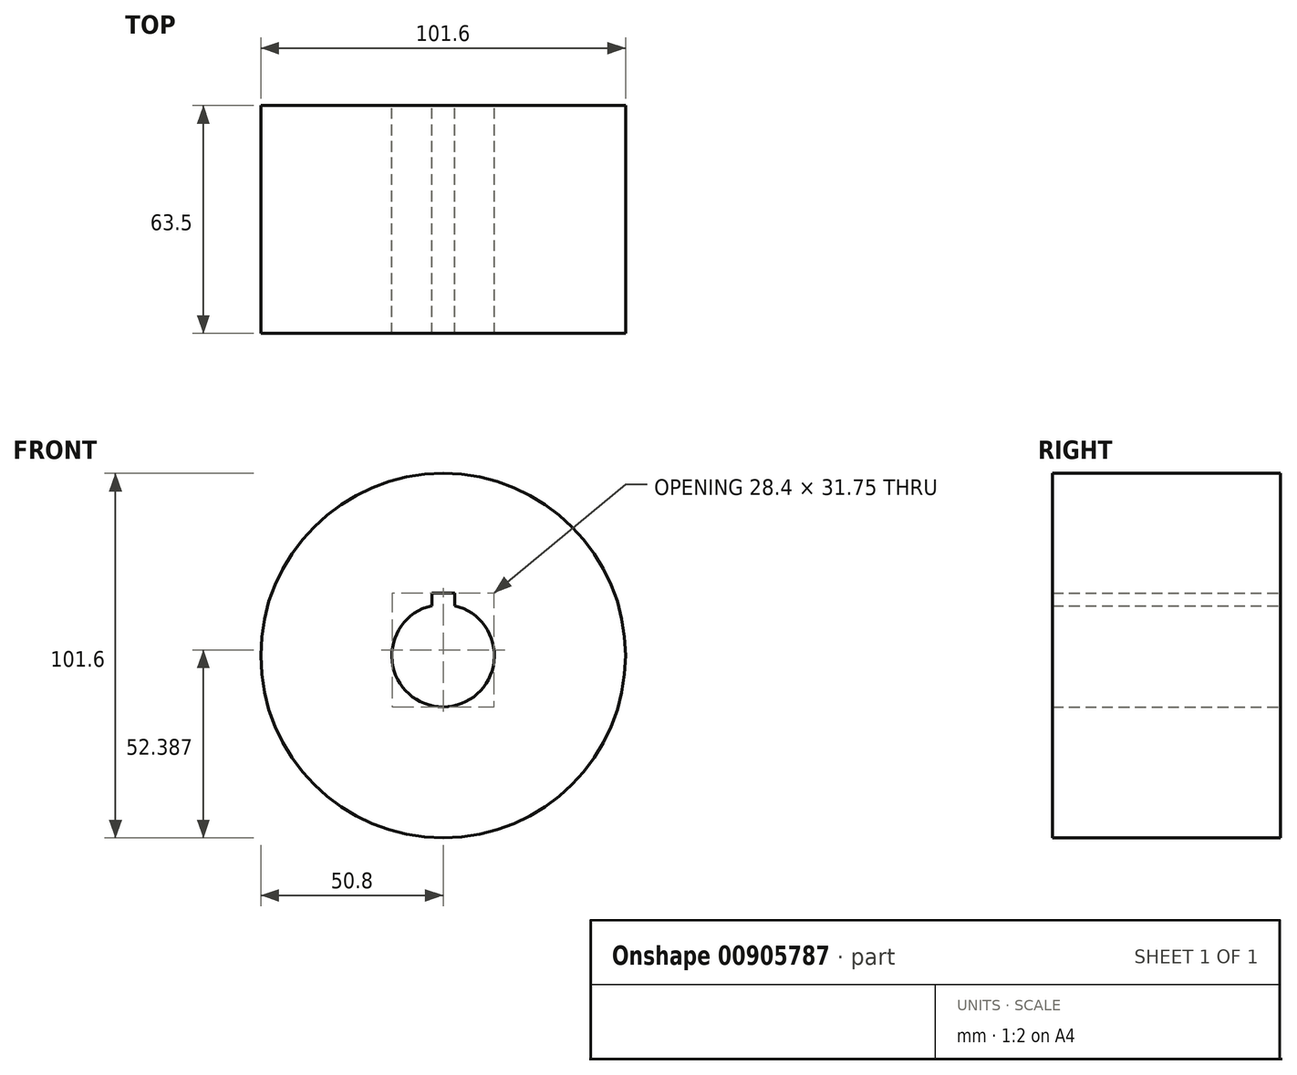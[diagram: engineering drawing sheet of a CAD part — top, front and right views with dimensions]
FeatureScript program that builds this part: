
annotation { "Feature Type Name" : "Feature", "Feature Type Description" : "" }
export const myFeature = defineFeature(function(context is Context, id is Id, definition is map)
    precondition{}
    {
        {
            var Q0;
            Q0=qCreatedBy(makeId("Front.planeOp"),FACE);
            var sketch = newSketch(context, id + "F0", { "sketchPlane" : qUnion([Q0])});
            skCircle(sketch, "E0", {"center": v(0, 0) * mm, "radius": 50.8 * mm});
            skArc(sketch, "E1", {"start": v(-3.18, 13.93) * mm, "mid": v(0, -14.29) * mm, "end": v(3.18, 13.93) * mm});
            skLineSegment(sketch, "E2.top", {"start": v(-3.18, 17.46) * mm, "end": v(3.18, 17.46) * mm});
            skLineSegment(sketch, "E2.left", {"start": v(-3.18, 13.93) * mm, "end": v(-3.18, 17.46) * mm});
            skLineSegment(sketch, "E2.right", {"start": v(3.17, 13.93) * mm, "end": v(3.17, 17.46) * mm});
            skPoint(sketch, "E3", {"position": v(0, -14.29) * mm});
            skSolve(sketch);
        }
        {
            var Q0;
            Q0=makeQuery(id+"F0.imprint","IMPRINT",FACE,{"disambiguationData":[TD([[makeQuery(id+"F0.imprint","IMPRINT",EDGE,{"derivedFrom":sQuery(id+"F0.wireOp",EDGE,"E0")}),1.0]])]});
            extrude(context, id + "F1", {"entities" : qUnion([Q0]), "depth" : 63.5 * mm, "offsetDistance" : 25.4 * mm});
        }
    });
